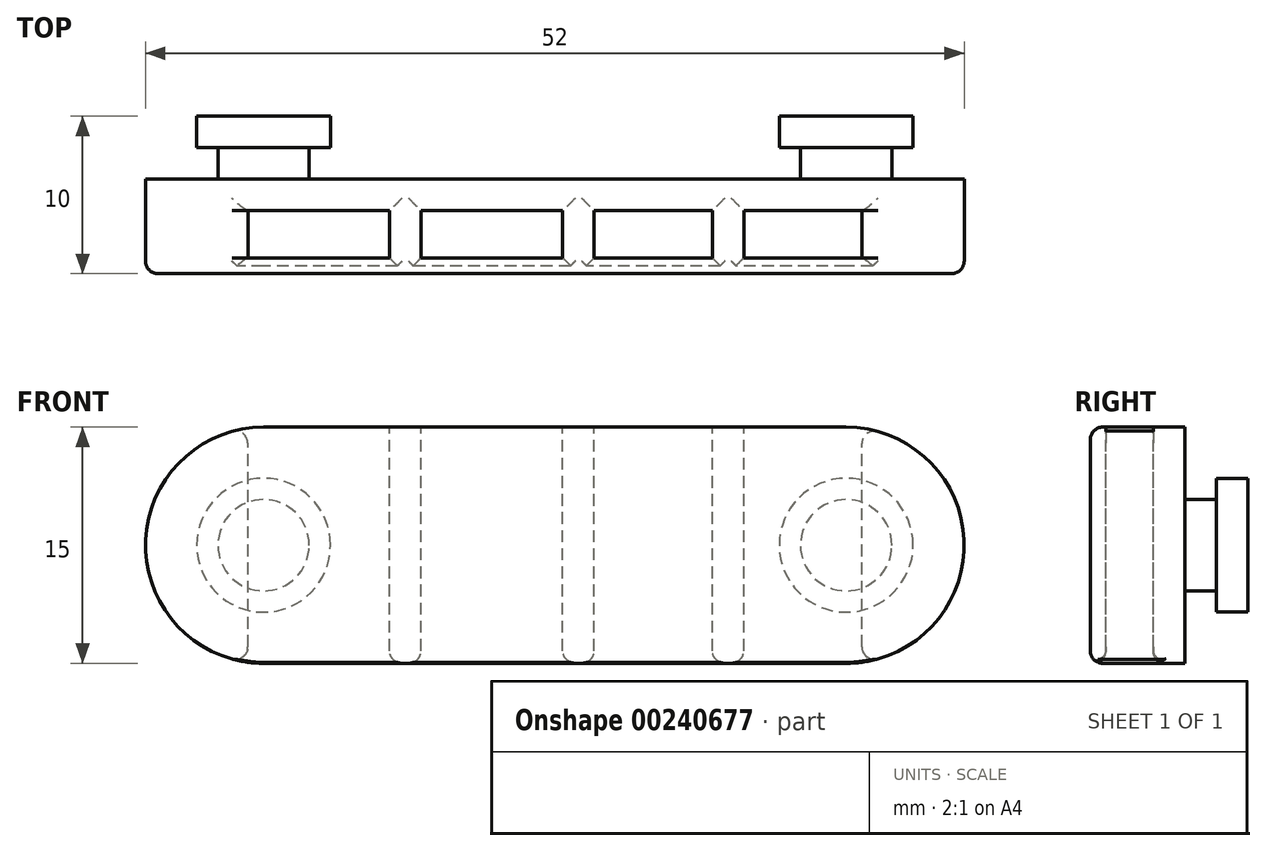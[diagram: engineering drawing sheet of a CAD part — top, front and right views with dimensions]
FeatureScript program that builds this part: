
annotation { "Feature Type Name" : "Feature", "Feature Type Description" : "" }
export const myFeature = defineFeature(function(context is Context, id is Id, definition is map)
    precondition{}
    {
        {
            var Q0;
            Q0=qCreatedBy(makeId("Front.planeOp"),FACE);
            var sketch = newSketch(context, id + "F0", { "sketchPlane" : qUnion([Q0])});
            skCircle(sketch, "E0", {"center": v(-18.5, 0) * mm, "radius": 2.9 * mm});
            skCircle(sketch, "E1", {"center": v(18.5, 0) * mm, "radius": 2.9 * mm});
            skArc(sketch, "E2", {"start": v(-18.5, 7.5) * mm, "mid": v(-26, 0) * mm, "end": v(-18.5, -7.5) * mm});
            skArc(sketch, "E3", {"start": v(18.5, -7.5) * mm, "mid": v(26, 0) * mm, "end": v(18.5, 7.5) * mm});
            skLineSegment(sketch, "E4", {"start": v(-18.5, 7.5) * mm, "end": v(18.5, 7.5) * mm});
            skLineSegment(sketch, "E5", {"start": v(-18.5, -7.5) * mm, "end": v(18.5, -7.5) * mm});
            skSolve(sketch);
        }
        {
            var Q0;
            Q0=makeQuery(id+"F0.imprint","IMPRINT",FACE,{"disambiguationData":[TD([[makeQuery(id+"F0.imprint","IMPRINT",EDGE,{"derivedFrom":sQuery(id+"F0.wireOp",EDGE,"E0")}),1.0]])]});
            var Q1;
            Q1=makeQuery(id+"F0.imprint","IMPRINT",FACE,{"disambiguationData":[TD([[makeQuery(id+"F0.imprint","IMPRINT",EDGE,{"derivedFrom":sQuery(id+"F0.wireOp",EDGE,"E1")}),1.0]])]});
            extrude(context, id + "F1", {"entities" : qUnion([Q0, Q1]), "oppositeDirection" : true, "depth" : 2 * mm});
        }
        {
            var Q0;
            Q0=makeQuery(id+"F0.imprint","IMPRINT",FACE,{"disambiguationData":[TD([[makeQuery(id+"F0.imprint","IMPRINT",EDGE,{"derivedFrom":sQuery(id+"F0.wireOp",EDGE,"E0")}),-1.0]])]});
            var Q1;
            Q1=makeQuery(id+"F0.imprint","IMPRINT",FACE,{"disambiguationData":[TD([[makeQuery(id+"F0.imprint","IMPRINT",EDGE,{"derivedFrom":sQuery(id+"F0.wireOp",EDGE,"E0")}),1.0]])]});
            var Q2;
            Q2=makeQuery(id+"F0.imprint","IMPRINT",FACE,{"disambiguationData":[TD([[makeQuery(id+"F0.imprint","IMPRINT",EDGE,{"derivedFrom":sQuery(id+"F0.wireOp",EDGE,"E1")}),1.0]])]});
            extrude(context, id + "F2", {"entities" : qUnion([Q0, Q1, Q2]), "operationType" : NewBodyOperationType.ADD, "depth" : 6 * mm});
        }
        {
            var Q0;
            Q0=makeQuery(id+"F2.opExtrude","SWEPT_FACE",FACE,{"disambiguationData":[OSD([sQuery(id+"F0.wireOp",EDGE,"E4")])]});
            var sketch = newSketch(context, id + "F3", { "sketchPlane" : qUnion([Q0])});
            skLineSegment(sketch, "E6.0", {"start": v(-18.5, -6) * mm, "end": v(18.5, -6) * mm, "construction": true});
            skLineSegment(sketch, "E7.0", {"start": v(-18.5, 0) * mm, "end": v(18.5, 0) * mm, "construction": true});
            skLineSegment(sketch, "E8.bottom", {"start": v(-19.5, -2) * mm, "end": v(-10.5, -2) * mm});
            skLineSegment(sketch, "E8.top", {"start": v(-19.5, -5) * mm, "end": v(-10.5, -5) * mm});
            skLineSegment(sketch, "E9.left", {"start": v(-19.5, -2) * mm, "end": v(-19.5, -5) * mm});
            skLineSegment(sketch, "E9.right", {"start": v(-10.5, -2) * mm, "end": v(-10.5, -5) * mm});
            skLineSegment(sketch, "E10.bottom", {"start": v(-8.5, -2) * mm, "end": v(0.5, -2) * mm});
            skLineSegment(sketch, "E10.top", {"start": v(-8.5, -5) * mm, "end": v(0.5, -5) * mm});
            skLineSegment(sketch, "E10.left", {"start": v(-8.5, -2) * mm, "end": v(-8.5, -5) * mm});
            skLineSegment(sketch, "E10.right", {"start": v(0.5, -2) * mm, "end": v(0.5, -5) * mm});
            skLineSegment(sketch, "E11.bottom", {"start": v(2.5, -2) * mm, "end": v(10, -2) * mm});
            skLineSegment(sketch, "E11.top", {"start": v(2.5, -5) * mm, "end": v(10, -5) * mm});
            skLineSegment(sketch, "E11.left", {"start": v(2.5, -2) * mm, "end": v(2.5, -5) * mm});
            skLineSegment(sketch, "E11.right", {"start": v(10, -2) * mm, "end": v(10, -5) * mm});
            skLineSegment(sketch, "E12.bottom", {"start": v(12, -2) * mm, "end": v(19.5, -2) * mm});
            skLineSegment(sketch, "E12.top", {"start": v(12, -5) * mm, "end": v(19.5, -5) * mm});
            skLineSegment(sketch, "E12.left", {"start": v(12, -2) * mm, "end": v(12, -5) * mm});
            skLineSegment(sketch, "E12.right", {"start": v(19.5, -2) * mm, "end": v(19.5, -5) * mm});
            skSolve(sketch);
        }
        {
            var Q0;
            Q0=makeQuery(id+"F3.imprint","IMPRINT",FACE,{"disambiguationData":[TD([[makeQuery(id+"F3.imprint","IMPRINT",EDGE,{"derivedFrom":sQuery(id+"F3.wireOp",EDGE,"E10.left")}),1.0]])]});
            var Q1;
            Q1=makeQuery(id+"F3.imprint","IMPRINT",FACE,{"disambiguationData":[TD([[makeQuery(id+"F3.imprint","IMPRINT",EDGE,{"derivedFrom":sQuery(id+"F3.wireOp",EDGE,"E11.left")}),1.0]])]});
            var Q2;
            {var subQ0=sQuery(id+"F3.wireOp",EDGE,"E9.left");Q2=makeQuery(id+"F3.imprint","IMPRINT",FACE,{"disambiguationData":[TD([[makeQuery(id+"F3.imprint","IMPRINT",EDGE,{"derivedFrom":subQ0}),1.0]])]});}
            var Q3;
            {var subQ0=sQuery(id+"F3.wireOp",EDGE,"E9.right");Q3=makeQuery(id+"F3.imprint","IMPRINT",FACE,{"disambiguationData":[TD([[makeQuery(id+"F3.imprint","IMPRINT",EDGE,{"derivedFrom":subQ0}),-1.0]])]});}
            var Q4;
            {var subQ0=sQuery(id+"F3.wireOp",EDGE,"E12.left");Q4=makeQuery(id+"F3.imprint","IMPRINT",FACE,{"disambiguationData":[TD([[makeQuery(id+"F3.imprint","IMPRINT",EDGE,{"derivedFrom":subQ0}),1.0]])]});}
            var Q5;
            {var subQ0=sQuery(id+"F3.wireOp",EDGE,"E12.right");Q5=makeQuery(id+"F3.imprint","IMPRINT",FACE,{"disambiguationData":[TD([[makeQuery(id+"F3.imprint","IMPRINT",EDGE,{"derivedFrom":subQ0}),-1.0]])]});}
            extrude(context, id + "F4", {"entities" : qUnion([Q0, Q1, Q2, Q3, Q4, Q5]), "operationType" : NewBodyOperationType.REMOVE, "endBound" : BoundingType.THROUGH_ALL, "oppositeDirection" : true, "depth" : 25 * mm});
        }
        {
            var Q0;
            Q0=makeQuery(id+"F1.opExtrude","CAP_FACE",FACE,{"disambiguationData":[OSD([sQuery(id+"F0.wireOp",EDGE,"E1")])],"isStart":false});
            var sketch = newSketch(context, id + "F5", { "sketchPlane" : qUnion([Q0])});
            skCircle(sketch, "E13.0.0", {"center": v(18.5, 0) * mm, "radius": 2.9 * mm});
            skCircle(sketch, "E14", {"center": v(-18.5, 0) * mm, "radius": 4.25 * mm});
            skCircle(sketch, "E15", {"center": v(18.5, 0) * mm, "radius": 4.25 * mm});
            skSolve(sketch);
        }
        {
            var Q0;
            Q0 = qSketchRegion(id + "F5", true);
            var Q1;
            Q1=makeQuery(id+"F5.imprint","IMPRINT",FACE,{"disambiguationData":[TD([[makeQuery(id+"F5.imprint","IMPRINT",EDGE,{"derivedFrom":sQuery(id+"F5.wireOp",EDGE,"E13.0.0")}),1.0]])]});
            extrude(context, id + "F6", {"entities" : qUnion([Q0, Q1]), "operationType" : NewBodyOperationType.ADD, "depth" : 2 * mm});
        }
        {
            var Q0;
            Q0=makeQuery(id+"F4.boolean.opBoolean","INTERSECT",EDGE,{"disambiguationData":[OD(0.0)],"derivedFrom":[makeQuery(id+"F2.opExtrude","SWEPT_FACE",FACE,{"disambiguationData":[OSD([sQuery(id+"F0.wireOp",EDGE,"E3")])]}),makeQuery(id+"F4.opExtrude","SWEPT_FACE",FACE,{"disambiguationData":[OSD([sQuery(id+"F3.wireOp",EDGE,"E12.right")])]})]});
            var Q1;
            Q1=makeQuery(id+"F4.boolean.opBoolean","COPY",EDGE,{"derivedFrom":makeQuery(id+"F4.opExtrude","CAP_EDGE",EDGE,{"disambiguationData":[OSD([sQuery(id+"F3.wireOp",EDGE,"E12.left")])],"isStart":true})});
            var Q2;
            Q2=makeQuery(id+"F4.boolean.opBoolean","COPY",EDGE,{"derivedFrom":makeQuery(id+"F4.opExtrude","CAP_EDGE",EDGE,{"disambiguationData":[OSD([sQuery(id+"F3.wireOp",EDGE,"E11.right")])],"isStart":true})});
            var Q3;
            Q3=makeQuery(id+"F4.boolean.opBoolean","COPY",EDGE,{"derivedFrom":makeQuery(id+"F4.opExtrude","CAP_EDGE",EDGE,{"disambiguationData":[OSD([sQuery(id+"F3.wireOp",EDGE,"E11.left")])],"isStart":true})});
            var Q4;
            Q4=makeQuery(id+"F4.boolean.opBoolean","COPY",EDGE,{"derivedFrom":makeQuery(id+"F4.opExtrude","CAP_EDGE",EDGE,{"disambiguationData":[OSD([sQuery(id+"F3.wireOp",EDGE,"E10.right")])],"isStart":true})});
            var Q5;
            Q5=makeQuery(id+"F4.boolean.opBoolean","COPY",EDGE,{"derivedFrom":makeQuery(id+"F4.opExtrude","CAP_EDGE",EDGE,{"disambiguationData":[OSD([sQuery(id+"F3.wireOp",EDGE,"E10.left")])],"isStart":true})});
            var Q6;
            Q6=makeQuery(id+"F4.boolean.opBoolean","COPY",EDGE,{"derivedFrom":makeQuery(id+"F4.opExtrude","CAP_EDGE",EDGE,{"disambiguationData":[OSD([sQuery(id+"F3.wireOp",EDGE,"E9.right")])],"isStart":true})});
            var Q7;
            Q7=makeQuery(id+"F4.boolean.opBoolean","INTERSECT",EDGE,{"disambiguationData":[OD(0.0)],"derivedFrom":[makeQuery(id+"F2.opExtrude","SWEPT_FACE",FACE,{"disambiguationData":[OSD([sQuery(id+"F0.wireOp",EDGE,"E2")])]}),makeQuery(id+"F4.opExtrude","SWEPT_FACE",FACE,{"disambiguationData":[OSD([sQuery(id+"F3.wireOp",EDGE,"E9.left")])]})]});
            var Q8;
            Q8=makeQuery(id+"F4.boolean.opBoolean","COPY",EDGE,{"derivedFrom":makeQuery(id+"F4.opExtrude","CAP_EDGE",EDGE,{"disambiguationData":[OSD([sQuery(id+"F3.wireOp",EDGE,"E12.top")])],"isStart":true})});
            var Q9;
            Q9=makeQuery(id+"F4.boolean.opBoolean","COPY",EDGE,{"derivedFrom":makeQuery(id+"F4.opExtrude","CAP_EDGE",EDGE,{"disambiguationData":[OSD([sQuery(id+"F3.wireOp",EDGE,"E12.bottom")])],"isStart":true})});
            var Q10;
            Q10=makeQuery(id+"F4.boolean.opBoolean","COPY",EDGE,{"derivedFrom":makeQuery(id+"F4.opExtrude","CAP_EDGE",EDGE,{"disambiguationData":[OSD([sQuery(id+"F3.wireOp",EDGE,"E11.top")])],"isStart":true})});
            var Q11;
            Q11=makeQuery(id+"F4.boolean.opBoolean","COPY",EDGE,{"derivedFrom":makeQuery(id+"F4.opExtrude","CAP_EDGE",EDGE,{"disambiguationData":[OSD([sQuery(id+"F3.wireOp",EDGE,"E11.bottom")])],"isStart":true})});
            var Q12;
            Q12=makeQuery(id+"F4.boolean.opBoolean","COPY",EDGE,{"derivedFrom":makeQuery(id+"F4.opExtrude","CAP_EDGE",EDGE,{"disambiguationData":[OSD([sQuery(id+"F3.wireOp",EDGE,"E10.bottom")])],"isStart":true})});
            var Q13;
            Q13=makeQuery(id+"F4.boolean.opBoolean","COPY",EDGE,{"derivedFrom":makeQuery(id+"F4.opExtrude","CAP_EDGE",EDGE,{"disambiguationData":[OSD([sQuery(id+"F3.wireOp",EDGE,"E10.top")])],"isStart":true})});
            var Q14;
            Q14=makeQuery(id+"F4.boolean.opBoolean","COPY",EDGE,{"derivedFrom":makeQuery(id+"F4.opExtrude","CAP_EDGE",EDGE,{"disambiguationData":[OSD([sQuery(id+"F3.wireOp",EDGE,"E8.top")])],"isStart":true})});
            var Q15;
            Q15=makeQuery(id+"F4.boolean.opBoolean","COPY",EDGE,{"derivedFrom":makeQuery(id+"F4.opExtrude","CAP_EDGE",EDGE,{"disambiguationData":[OSD([sQuery(id+"F3.wireOp",EDGE,"E8.bottom")])],"isStart":true})});
            var Q16;
            Q16=makeQuery(id+"F2.opExtrude","CAP_EDGE",EDGE,{"disambiguationData":[OSD([sQuery(id+"F0.wireOp",EDGE,"E2")])],"isStart":false});
            var Q17;
            Q17=makeQuery(id+"F4.boolean.opBoolean","INTERSECT",EDGE,{"derivedFrom":[makeQuery(id+"F2.opExtrude","SWEPT_FACE",FACE,{"disambiguationData":[OSD([sQuery(id+"F0.wireOp",EDGE,"E5")])]}),makeQuery(id+"F4.opExtrude","SWEPT_FACE",FACE,{"disambiguationData":[OSD([sQuery(id+"F3.wireOp",EDGE,"E12.top")])]})]});
            var Q18;
            Q18=makeQuery(id+"F4.boolean.opBoolean","INTERSECT",EDGE,{"disambiguationData":[OD(1.0)],"derivedFrom":[makeQuery(id+"F2.opExtrude","SWEPT_FACE",FACE,{"disambiguationData":[OSD([sQuery(id+"F0.wireOp",EDGE,"E3")])]}),makeQuery(id+"F4.opExtrude","SWEPT_FACE",FACE,{"disambiguationData":[OSD([sQuery(id+"F3.wireOp",EDGE,"E12.right")])]})]});
            var Q19;
            Q19=makeQuery(id+"F4.boolean.opBoolean","INTERSECT",EDGE,{"derivedFrom":[makeQuery(id+"F2.opExtrude","SWEPT_FACE",FACE,{"disambiguationData":[OSD([sQuery(id+"F0.wireOp",EDGE,"E5")])]}),makeQuery(id+"F4.opExtrude","SWEPT_FACE",FACE,{"disambiguationData":[OSD([sQuery(id+"F3.wireOp",EDGE,"E12.bottom")])]})]});
            var Q20;
            Q20=makeQuery(id+"F4.boolean.opBoolean","INTERSECT",EDGE,{"derivedFrom":[makeQuery(id+"F2.opExtrude","SWEPT_FACE",FACE,{"disambiguationData":[OSD([sQuery(id+"F0.wireOp",EDGE,"E5")])]}),makeQuery(id+"F4.opExtrude","SWEPT_FACE",FACE,{"disambiguationData":[OSD([sQuery(id+"F3.wireOp",EDGE,"E12.left")])]})]});
            var Q21;
            Q21=makeQuery(id+"F4.boolean.opBoolean","INTERSECT",EDGE,{"derivedFrom":[makeQuery(id+"F2.opExtrude","SWEPT_FACE",FACE,{"disambiguationData":[OSD([sQuery(id+"F0.wireOp",EDGE,"E5")])]}),makeQuery(id+"F4.opExtrude","SWEPT_FACE",FACE,{"disambiguationData":[OSD([sQuery(id+"F3.wireOp",EDGE,"E11.right")])]})]});
            var Q22;
            Q22=makeQuery(id+"F4.boolean.opBoolean","INTERSECT",EDGE,{"derivedFrom":[makeQuery(id+"F2.opExtrude","SWEPT_FACE",FACE,{"disambiguationData":[OSD([sQuery(id+"F0.wireOp",EDGE,"E5")])]}),makeQuery(id+"F4.opExtrude","SWEPT_FACE",FACE,{"disambiguationData":[OSD([sQuery(id+"F3.wireOp",EDGE,"E11.bottom")])]})]});
            var Q23;
            Q23=makeQuery(id+"F4.boolean.opBoolean","INTERSECT",EDGE,{"derivedFrom":[makeQuery(id+"F2.opExtrude","SWEPT_FACE",FACE,{"disambiguationData":[OSD([sQuery(id+"F0.wireOp",EDGE,"E5")])]}),makeQuery(id+"F4.opExtrude","SWEPT_FACE",FACE,{"disambiguationData":[OSD([sQuery(id+"F3.wireOp",EDGE,"E11.left")])]})]});
            var Q24;
            Q24=makeQuery(id+"F4.boolean.opBoolean","INTERSECT",EDGE,{"derivedFrom":[makeQuery(id+"F2.opExtrude","SWEPT_FACE",FACE,{"disambiguationData":[OSD([sQuery(id+"F0.wireOp",EDGE,"E5")])]}),makeQuery(id+"F4.opExtrude","SWEPT_FACE",FACE,{"disambiguationData":[OSD([sQuery(id+"F3.wireOp",EDGE,"E11.top")])]})]});
            var Q25;
            Q25=makeQuery(id+"F4.boolean.opBoolean","INTERSECT",EDGE,{"derivedFrom":[makeQuery(id+"F2.opExtrude","SWEPT_FACE",FACE,{"disambiguationData":[OSD([sQuery(id+"F0.wireOp",EDGE,"E5")])]}),makeQuery(id+"F4.opExtrude","SWEPT_FACE",FACE,{"disambiguationData":[OSD([sQuery(id+"F3.wireOp",EDGE,"E10.right")])]})]});
            var Q26;
            Q26=makeQuery(id+"F4.boolean.opBoolean","INTERSECT",EDGE,{"derivedFrom":[makeQuery(id+"F2.opExtrude","SWEPT_FACE",FACE,{"disambiguationData":[OSD([sQuery(id+"F0.wireOp",EDGE,"E5")])]}),makeQuery(id+"F4.opExtrude","SWEPT_FACE",FACE,{"disambiguationData":[OSD([sQuery(id+"F3.wireOp",EDGE,"E10.bottom")])]})]});
            var Q27;
            Q27=makeQuery(id+"F4.boolean.opBoolean","INTERSECT",EDGE,{"derivedFrom":[makeQuery(id+"F2.opExtrude","SWEPT_FACE",FACE,{"disambiguationData":[OSD([sQuery(id+"F0.wireOp",EDGE,"E5")])]}),makeQuery(id+"F4.opExtrude","SWEPT_FACE",FACE,{"disambiguationData":[OSD([sQuery(id+"F3.wireOp",EDGE,"E10.left")])]})]});
            var Q28;
            Q28=makeQuery(id+"F4.boolean.opBoolean","INTERSECT",EDGE,{"derivedFrom":[makeQuery(id+"F2.opExtrude","SWEPT_FACE",FACE,{"disambiguationData":[OSD([sQuery(id+"F0.wireOp",EDGE,"E5")])]}),makeQuery(id+"F4.opExtrude","SWEPT_FACE",FACE,{"disambiguationData":[OSD([sQuery(id+"F3.wireOp",EDGE,"E10.top")])]})]});
            var Q29;
            Q29=makeQuery(id+"F4.boolean.opBoolean","INTERSECT",EDGE,{"derivedFrom":[makeQuery(id+"F2.opExtrude","SWEPT_FACE",FACE,{"disambiguationData":[OSD([sQuery(id+"F0.wireOp",EDGE,"E5")])]}),makeQuery(id+"F4.opExtrude","SWEPT_FACE",FACE,{"disambiguationData":[OSD([sQuery(id+"F3.wireOp",EDGE,"E9.right")])]})]});
            var Q30;
            Q30=makeQuery(id+"F4.boolean.opBoolean","INTERSECT",EDGE,{"derivedFrom":[makeQuery(id+"F2.opExtrude","SWEPT_FACE",FACE,{"disambiguationData":[OSD([sQuery(id+"F0.wireOp",EDGE,"E5")])]}),makeQuery(id+"F4.opExtrude","SWEPT_FACE",FACE,{"disambiguationData":[OSD([sQuery(id+"F3.wireOp",EDGE,"E8.bottom")])]})]});
            var Q31;
            Q31=makeQuery(id+"F4.boolean.opBoolean","INTERSECT",EDGE,{"disambiguationData":[OD(1.0)],"derivedFrom":[makeQuery(id+"F2.opExtrude","SWEPT_FACE",FACE,{"disambiguationData":[OSD([sQuery(id+"F0.wireOp",EDGE,"E2")])]}),makeQuery(id+"F4.opExtrude","SWEPT_FACE",FACE,{"disambiguationData":[OSD([sQuery(id+"F3.wireOp",EDGE,"E9.left")])]})]});
            var Q32;
            Q32=makeQuery(id+"F4.boolean.opBoolean","INTERSECT",EDGE,{"derivedFrom":[makeQuery(id+"F2.opExtrude","SWEPT_FACE",FACE,{"disambiguationData":[OSD([sQuery(id+"F0.wireOp",EDGE,"E5")])]}),makeQuery(id+"F4.opExtrude","SWEPT_FACE",FACE,{"disambiguationData":[OSD([sQuery(id+"F3.wireOp",EDGE,"E8.top")])]})]});
            fillet(context, id + "F7", {"entities" : qUnion([Q0, Q1, Q2, Q3, Q4, Q5, Q6, Q7, Q8, Q9, Q10, Q11, Q12, Q13, Q14, Q15, Q16, Q17, Q18, Q19, Q20, Q21, Q22, Q23, Q24, Q25, Q26, Q27, Q28, Q29, Q30, Q31, Q32]), "radius" : 0.8 * mm, "tangentPropagation" : true, "allowEdgeOverflow" : false});
        }
    });
